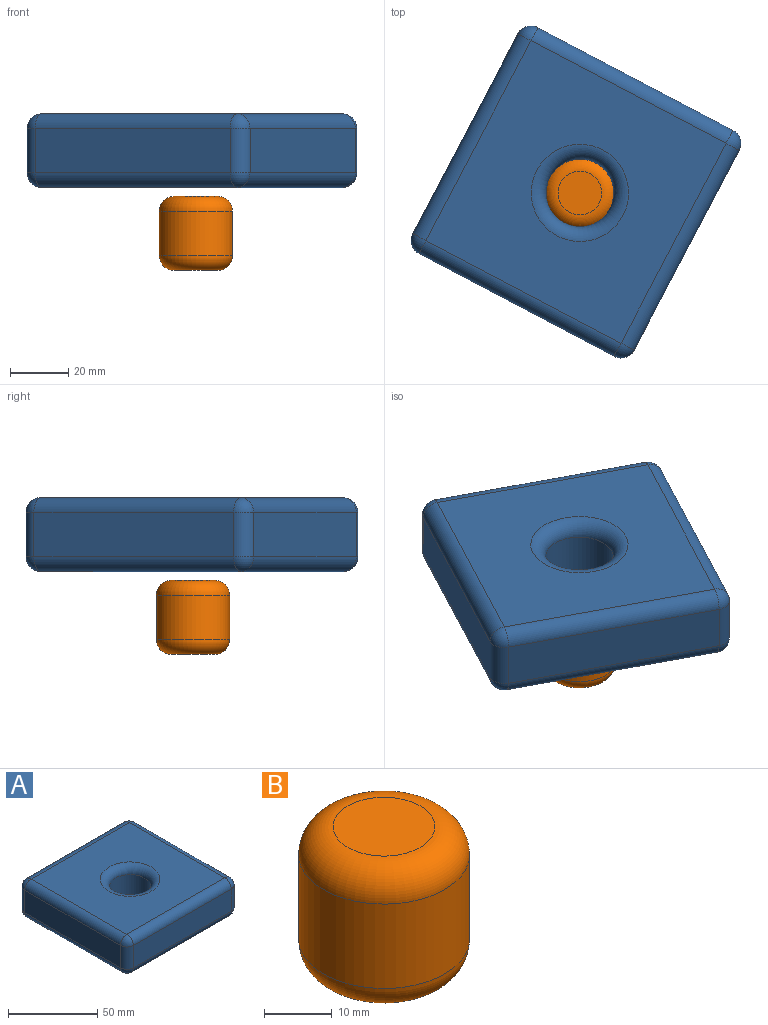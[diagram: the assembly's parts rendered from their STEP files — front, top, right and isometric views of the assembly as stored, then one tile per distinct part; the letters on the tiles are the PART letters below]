
ASSEMBLY  parts=2 mates=1
PART A: 29 faces, bbox 87.7x85.9x25.4 mm
  f0: plane 77.57x15.24mm, normal (0,1,0), area 1182.2mm2, adj f8,f11,f19,f25
  f1: plane 75.78x15.24mm, normal (-1,0,0), area 1154.9mm2, adj f9,f11,f14,f21
  f2: plane 77.57x15.24mm, normal (0,-1,0), area 1182.2mm2, adj f12,f14,f15,f22
  f3: plane 75.78x15.24mm, normal (1,0,0), area 1154.9mm2, adj f15,f17,f19,f26
  f4: plane 77.57x75.78mm, normal (0,0,1), area 5000.9mm2, adj f7,f8,f9,f12,f17
  f5: plane 77.57x75.78mm, normal (0,0,-1), area 5000.9mm2, adj f21,f22,f25,f26,f28
  f6: cylinder r=11.63mm len=23.27mm, axis (0,0,1), area 1113.9mm2, adj f7,f28
  f7: torus R=16.71mm, axis (0,0,1), area 675.8mm2, adj f4,f6
  f8: cylinder r=5.08mm len=77.57mm, axis (1,0,0), area 619mm2, adj f0,f4,f10,f18
  f9: cylinder r=5.08mm len=75.78mm, axis (0,1,0), area 604.7mm2, adj f1,f4,f10,f13
  f10: sphere r=5.08mm, area 40.5mm2, adj f8,f9,f11
  f11: cylinder r=5.08mm len=15.24mm, axis (0,0,1), area 121.6mm2, adj f0,f1,f10,f23
  f12: cylinder r=5.08mm len=77.57mm, axis (-1,0,0), area 619mm2, adj f2,f4,f13,f16
  f13: sphere r=5.08mm, area 40.5mm2, adj f9,f12,f14
  f14: cylinder r=5.08mm len=15.24mm, axis (0,0,-1), area 121.6mm2, adj f1,f2,f13,f20
  f15: cylinder r=5.08mm len=15.24mm, axis (0,0,1), area 121.6mm2, adj f2,f3,f16,f24
  f16: sphere r=5.08mm, area 40.5mm2, adj f12,f15,f17
  f17: cylinder r=5.08mm len=75.78mm, axis (0,-1,0), area 604.7mm2, adj f3,f4,f16,f18
  f18: sphere r=5.08mm, area 40.5mm2, adj f8,f17,f19
  f19: cylinder r=5.08mm len=15.24mm, axis (0,0,-1), area 121.6mm2, adj f0,f3,f18,f27
  f20: sphere r=5.08mm, area 40.5mm2, adj f14,f21,f22
  f21: cylinder r=5.08mm len=75.78mm, axis (0,-1,0), area 604.7mm2, adj f1,f5,f20,f23
  f22: cylinder r=5.08mm len=77.57mm, axis (1,0,0), area 619mm2, adj f2,f5,f20,f24
  f23: sphere r=5.08mm, area 40.5mm2, adj f11,f21,f25
  f24: sphere r=5.08mm, area 40.5mm2, adj f15,f22,f26
  f25: cylinder r=5.08mm len=77.57mm, axis (-1,0,0), area 619mm2, adj f0,f5,f23,f27
  f26: cylinder r=5.08mm len=75.78mm, axis (0,1,0), area 604.7mm2, adj f3,f5,f24,f27
  f27: sphere r=5.08mm, area 40.5mm2, adj f19,f25,f26
  f28: torus R=16.71mm, axis (0,0,1), area 675.8mm2, adj f5,f6
PART B: 5 faces, bbox 27.3x27.3x25.4 mm
  f0: cylinder r=12.59mm len=25.19mm, axis (0,0,-1), area 1205.9mm2, adj f3,f4
  f1: plane 15.03x15.03mm, normal (0,0,1), area 177.4mm2, adj f3
  f2: plane 15.03x15.03mm, normal (0,0,-1), area 177.4mm2, adj f4
  f3: torus R=7.51mm, axis (0,0,1), area 538.9mm2, adj f0,f1
  f4: torus R=7.51mm, axis (0,0,1), area 538.9mm2, adj f0,f2
PLACE A rot(axis=(0,0,1),62.2deg) t=(-12.74,-22.33,1.46)mm
PLACE B rot(axis=(0,0,1),15.8deg) t=(-12.74,-22.33,-26.98)mm fixed
MATE cylindrical A.f6 <-> B.f0  axis (0,0,1) through (-12.74,-22.33,25.37)mm
